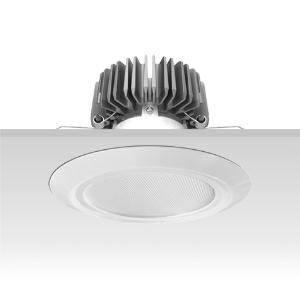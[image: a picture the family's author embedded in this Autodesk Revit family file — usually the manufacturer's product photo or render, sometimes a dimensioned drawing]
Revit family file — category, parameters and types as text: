
# Revit family: 3f_filippi_-_3f_reno_bianco_ampio_3f_filippi_-_30691_a01048_-_3f_reno_200_wh_4000-930_dali_wide___smp_wh_4679
name_source: partatom
category: Lighting Fixtures
units: mm (PartAtom-declared; Revit-internal decimal feet)

## family parameters
Cut with Voids When Loaded = No
Host = Face
Light Source = No
Part Type = Normal
Room Calculation Point = No
Round Connector Dimension = Use Diameter
Shared = No

## types (1)
- 3F Filippi - 3F Reno Bianco Ampio (1 x LED, 2801 lm, 43 W, 3000 K)
    Apparent Load = 43 VA
    Approval mark = CE
    CIE Flux Codes = 74 92 98 100 100
    Color Rendering = 90
    Color Temperature = 3000 K
    Control Gear = Electronic transformer
    Default Elevation = 1800 mm
    Description = ILLUMINOTECHNICAL
Luminous efficiency 100% (DLOR 100%, ULOR 0%).
Initial luminous flux of the luminaire 2801 lm.
Direct symmetric wide distribution.
Installation Interdistance Transv.D = 1.06 x hu - Long.D = 1.04 x hu.
Tabular UGR (CIE 117 - 4H-8H; S=0.25H; 70/50/20): RUG 23.1 - 23.
Beam angle: 70° - 69°.
Luminous efficacy 65 lm/W.
Lifetime (L90/B10): 30000 h. (tq+25°C)
Lifetime (L85/B10): 50000 h. (tq+25°C)
Lifetime (L70/B10): 80000 h. (tq+25°C)
Sudden decreased luminous flux after 50000 hours: 0% (C0).
Photobiological safety in compliance with IEC/TR 62778: RG1 low risk, (IEC 62471).
In compliance with IEC/EN 62722-2-1 - IEC/EN 62717 standards.

SOURCE
Compact LED module 4000/930.
Energy efficiency class (UE 2019/2020 - UE 2019/2015): F.
CIE 13.3 Colour rendering index: CRI >90 (R9 >50%).
IES TM-30 Fidelity Index: Rf = 92 Rg = 101.
CCT nominal colour temperature 3000 K.
Colour initial tolerance (MacAdam): SDCM 3.
Zhaga Book 3 compliant.

MECHANICAL
Passive heat dissipator in die-casting aluminium, oversized, for optimum thermal management of the LED module.
Parabolic element with graduated/concentric rings in white polycarbonate.
Transparent external lens with glossy and satin differentiated surfaces, with a cooling and anti-insect system in methacrylate (PMMA).
Fastening spring clips in stainless steel.
Dimensions: diameter 226 mm, height 146 mm. Weight 1.725 kg.
IP44 protection degree for exposed part, IP20 for recessed part.
Mechanical strength to impacts IK05 (0.7 joule).
Glow-wire test resistance 650°C.

ELECTRICAL
Wiring on a separate unit.
Halogen Free DALI-2 DATI (Parts 251, 252, 253), PUSH-DIM, electronic wiring 230V-50/60Hz, power factor 0.97 at full load, THD <25%, constant output current, SELV, class II, 1 driver, 1 DALI addresse.
Power of the luminaire 43 W.
ENEC - CE.
SAFE FLICKER: PstLM=<1 and SVM=<0.4 (IEC TR 61547-1 and IEC TR 63158), to ensure a more comfortable and safe light.
Luminaire compliant with EN 60598-2-22 for power supply from a centralised emergency system CPSS (Central Power Supply System), not incorporated in the luminaire - high risk areas excluded. The default power and flux are 100% in AC and 100% in DC.
Ambient temperature from 0°C to +25°C.
Temperature class T6 max 85°C.
Relative humidity UR: <85%.

INSTALLATION
Pull-up recessed fitting.
False ceiling carving: 200 mm.
All accessories dedicated to this product are available on the Catalog and on our website www.3F-Filippi.com.

ACCESSORIES
A01048 - Anti-glare microprismatic SMP diffuser in methacrylate (PMMA), locked and in line with the trim, in white polycarbonate.

APPLICATIONS
Suitable product for food production plants (HACCP), IFS (Food Version 6), BRC (GSFS Food Version 7).
Environments: architectural, commercial, exhibition areas, transit areas, corridors, shops, display windows, service areas.
In false ceilings with narrow voids.

LIGHT MANAGEMENT
Recommended minimum setting: 10%.
The luminaire, equipped with (DALI-2 DATI) driver, can be controlled manually with 3F Easy Dim technology or automatically/manually with wired or wireless DALI/D2D control systems.
The D2D driver guarantees interoperability with other devices with the same certification by making the following information available:
Device Data (Part 251), Energy Report (Part 252), Diagnosis & Maintenance (Part 253).
In electrical systems without a regulation system (manual or automatic) and DALI bus, a suitable jumper must be made on the DA-DA terminals of the appliance.

WARNING
Luminaire designed for disposal/recycling at end-of-life.
Replaceable (LED only) light source by a professional. Replaceable control gear by a professional.
    Height = 0 mm  [stored 0 ft]
    Lamp = 1 x LED
    Lamp Light Flux = 2801 lm
    Lamp Power = 43 W
    Lamp count = 1
    Length = 226 mm
    Lifetime = 50000 h
    Luminous efficacy = 65 lm/W
    Manufacturer = 3F Filippi
    ModVariant = No
    Model = 3F Filippi - 30691+A01048 - 3F Reno 200 WH 4000-930 DALI WIDE + SMP WH
    Mounting Place = Ceiling
    Mounting Type = Recessed
    Number of Poles = 1
    OnlyDefault = Yes
    Power Factor = 1
    Product Name = 3F Filippi - 3F Reno Bianco Ampio
    Product group = recessed luminaire
    ProductGroupID = 4
    Protection Class = Protection class II
    Protection Degree = IP 20
    RLX_Detail_Level = 1
    RLX_Emergency_Light_Flux = 0 lm
    RLX_Emergency_Type = 0
    RLX_Emergency_Type_DB = No
    RlxData = <blob elided: 97685 chars, md5=019763d7>
    Socket = socket
    Standby Power = 0 W
    System Light Flux = 2801 lm
    System Power = 43 W
    Type Comments = Product without accessories
    Type Image = 3ffilippi_3f_reno_200_wh_vs_smp.jpg
    URL = http://relux.com
    VarID = ---
    Voltage = 0 V
    Weight = 0.00 kg
    Width = 0 mm  [stored 0 ft]

note: [stored X ft] marks values corroborated as IEEE doubles in the binary element streams (Revit-internal decimal feet)

## geometry (parser evidence)
native form markers: Blend x4, Sweep x11
no freeform markers — native parametric forms only
